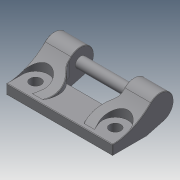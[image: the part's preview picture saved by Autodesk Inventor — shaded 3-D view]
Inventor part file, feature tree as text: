
AUTODESK INVENTOR PART (.ipt)
format: ipt  version: 2020.3 (Build 243373000, 373)  size: 313,344 bytes
history: native  units: in
note: dims shown in document units (in); Inventor stores cm internally (conversion verified against a paired STEP export)
features: fillet x2, revolve x1
ambient origin geometry x8: Origin, YZ Plane, XZ Plane, XY Plane, X Axis, Y Axis, Z Axis, Center Point
bodies: Solid1 (feature_tree), Solid2 (feature_tree), Solid3 (feature_tree)
feature tree (3):
  fillet  "Fillet5"  [1 undecoded]
  fillet  "Fillet4"  [1 undecoded]
  revolve  "Revolve1"  [1 undecoded]
note: 3 required parameter values undecoded (feature->parameter linkage not recoverable at this tier; creation-order binding heuristic only, values carry confidence <= 0.55)
